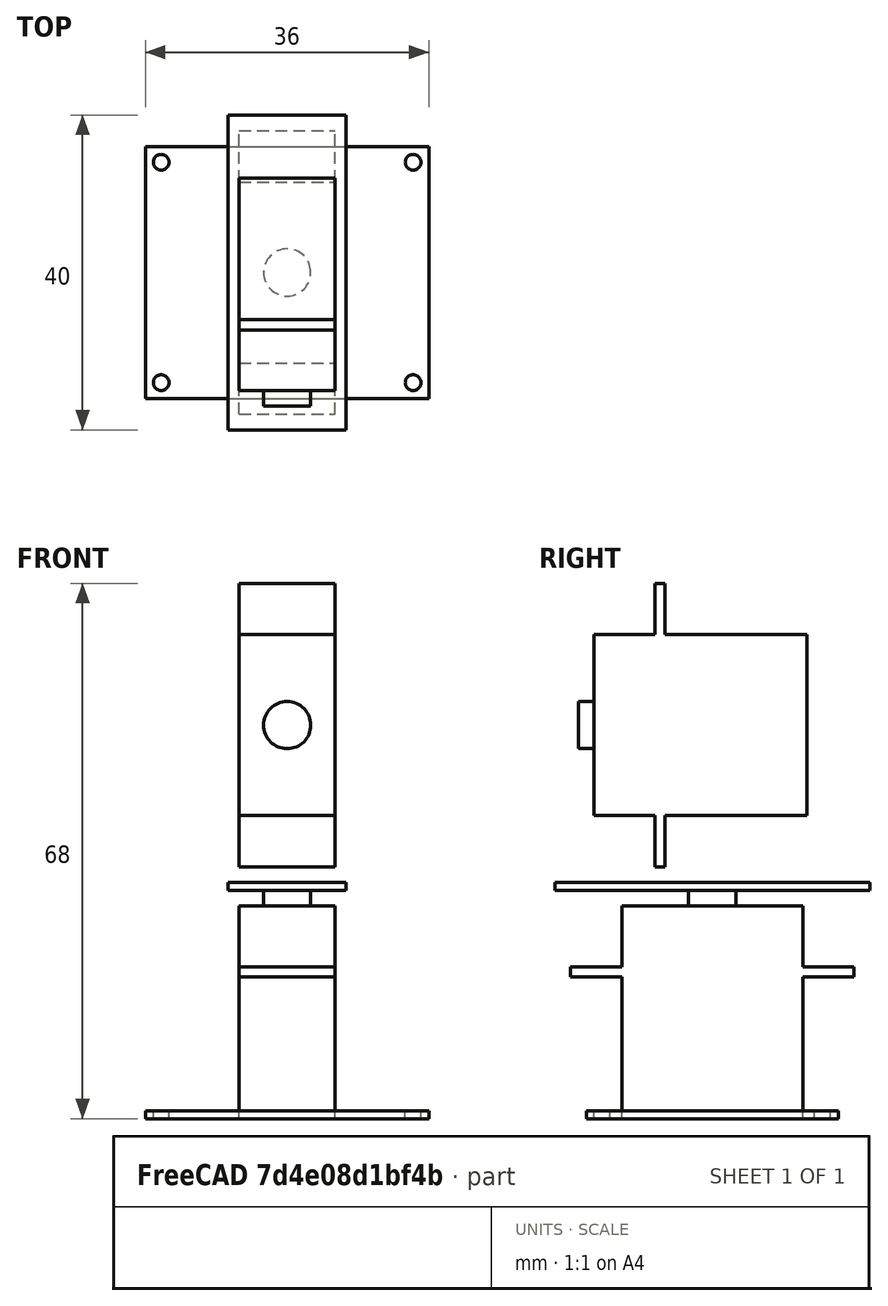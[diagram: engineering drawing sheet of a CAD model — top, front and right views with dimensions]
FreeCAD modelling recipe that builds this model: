
FCSTD DOCUMENT  (FreeCAD 0.18R16146 (Git))
Label: gyro_scope_model
License: All rights reserved
LicenseURL: http://en.wikipedia.org/wiki/All_rights_reserved
objects: Part::Box×8, Part::Cylinder×6, Part::MultiFuse×3, Part::Cut×1
note: 18 computed .brp shape members not serialized (recipe doc carries the construction recipe); baked Part::Feature solids carry a one-line shape summary decoded from their .brp

FEATURE [Part::Box] Box  label="Base"
  AttacherType = Attacher::AttachEngine3D
  Height = 1
  Length = 36
  Placement = pos=(-18,-16,0) rot=(0,0,1;0rad)
  Width = 32
FEATURE [Part::Cylinder] Cylinder  label="hole"
  Angle = 360
  AttacherType = Attacher::AttachEngine3D
  Height = 1
  Placement = pos=(-16,-14,0) rot=(0,0,1;0rad)
  Radius = 1
FEATURE [Part::Cylinder] Cylinder001  label="hole2"
  Angle = 360
  AttacherType = Attacher::AttachEngine3D
  Height = 1
  Placement = pos=(-16,14,0) rot=(0,0,1;0rad)
  Radius = 1
FEATURE [Part::Cylinder] Cylinder002  label="hole3"
  Angle = 360
  AttacherType = Attacher::AttachEngine3D
  Height = 1
  Placement = pos=(16,14,0) rot=(0,0,1;0rad)
  Radius = 1
FEATURE [Part::Cylinder] Cylinder003  label="hole4"
  Angle = 360
  AttacherType = Attacher::AttachEngine3D
  Height = 1
  Placement = pos=(16,-14,0) rot=(0,0,1;0rad)
  Radius = 1
FEATURE [Part::MultiFuse] Fusion  label="Holes"
  Shapes = -> [Cylinder003,Cylinder001,Cylinder,Cylinder002]
FEATURE [Part::Cut] Cut  label="Base with attachment holes"
  Base = -> Box
  Tool = -> Fusion
FEATURE [Part::Box] Box001  label="body"
  AttacherType = Attacher::AttachEngine3D
  Height = 27
  Length = 12.2
  Placement = pos=(-6.1,-11.5,0) rot=(0,0,1;0rad)
  Width = 23
FEATURE [Part::Box] Box002  label="right shelf"
  AttacherType = Attacher::AttachEngine3D
  Height = 1.3
  Length = 12.2
  Placement = pos=(-6.1,11.5,18) rot=(0,0,1;0rad)
  Width = 6.5
FEATURE [Part::Box] Box003  label="left shelf"
  AttacherType = Attacher::AttachEngine3D
  Height = 1.3
  Length = 12.2
  Placement = pos=(-6.1,-18,18) rot=(0,0,1;0rad)
  Width = 6.5
FEATURE [Part::Cylinder] Cylinder004  label="rotation cylinder"
  Angle = 360
  AttacherType = Attacher::AttachEngine3D
  Height = 2
  Placement = pos=(0,0,27) rot=(0,0,1;0rad)
  Radius = 3
FEATURE [Part::MultiFuse] Fusion001  label="Base servo motor"
  Shapes = -> [Box002,Cylinder004,Box003,Box001]
FEATURE [Part::Box] Box004  label="Rotating base"
  AttacherType = Attacher::AttachEngine3D
  Height = 1
  Length = 15
  Placement = pos=(-7.5,-20,29) rot=(0,0,1;0rad)
  Width = 40
FEATURE [Part::Cylinder] Cylinder005  label="rotation cylinder001"
  Angle = 360
  AttacherType = Attacher::AttachEngine3D
  Height = 2
  Placement = pos=(0,0,27) rot=(0,0,1;0rad)
  Radius = 3
FEATURE [Part::Box] Box005  label="left shelf001"
  AttacherType = Attacher::AttachEngine3D
  Height = 1.3
  Length = 12.2
  Placement = pos=(-6.1,-18,18) rot=(0,0,1;0rad)
  Width = 6.5
FEATURE [Part::Box] Box006  label="right shelf001"
  AttacherType = Attacher::AttachEngine3D
  Height = 1.3
  Length = 12.2
  Placement = pos=(-6.1,11.5,18) rot=(0,0,1;0rad)
  Width = 6.5
FEATURE [Part::Box] Box007  label="body001"
  AttacherType = Attacher::AttachEngine3D
  Height = 27
  Length = 12.2
  Placement = pos=(-6.1,-11.5,0) rot=(0,0,1;0rad)
  Width = 23
FEATURE [Part::MultiFuse] Fusion002  label="Upper servo motor"
  Placement = pos=(0,12,50) rot=(0,0.707107,-0.707107;3.14159rad)
  Shapes = -> [Box006,Cylinder005,Box005,Box007]
